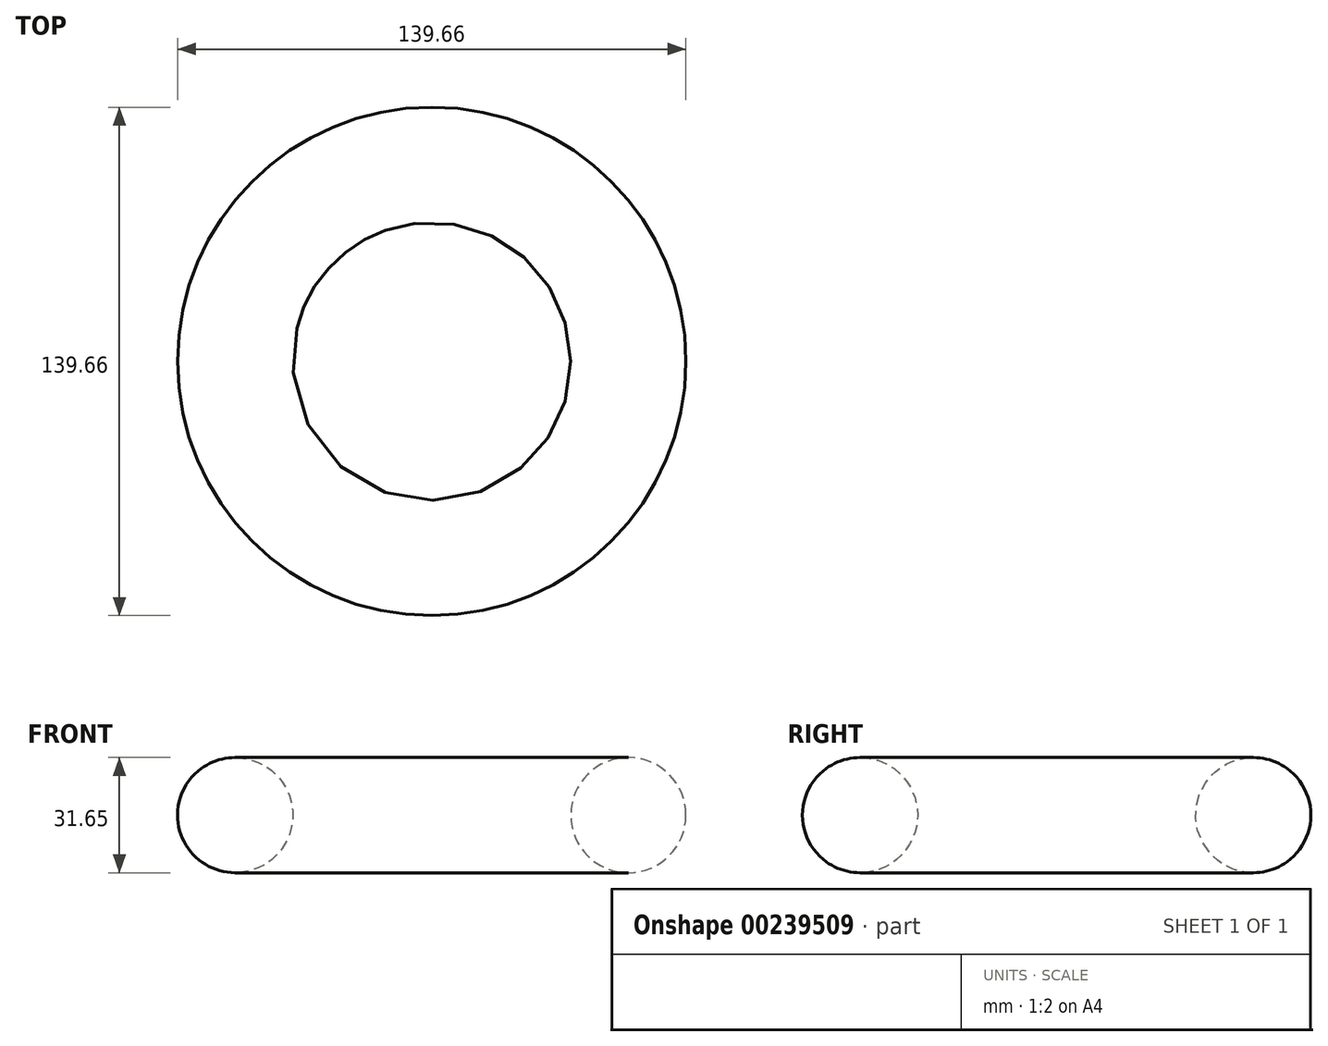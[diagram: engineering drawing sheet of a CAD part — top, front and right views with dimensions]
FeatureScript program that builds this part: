
annotation { "Feature Type Name" : "Feature", "Feature Type Description" : "" }
export const myFeature = defineFeature(function(context is Context, id is Id, definition is map)
    precondition{}
    {
        {
            var Q0;
            Q0=qCreatedBy(makeId("Front.planeOp"),FACE);
            var sketch = newSketch(context, id + "F0", { "sketchPlane" : qUnion([Q0])});
            skCircle(sketch, "E0", {"center": v(54, 10.16) * mm, "radius": 15.82 * mm});
            skLineSegment(sketch, "E1", {"start": v(0, 58.1) * mm, "end": v(0, -35.65) * mm, "construction": true});
            skSolve(sketch);
        }
        {
            var Q0;
            Q0 = qSketchRegion(id + "F0", true);
            var Q1;
            Q1=sQuery(id+"F0.wireOp",EDGE,"E1");
            revolve(context, id + "F1", {"entities" : qUnion([Q0]), "axis" : qUnion([Q1]), "revolveType" : RevolveType.FULL});
        }
    });
